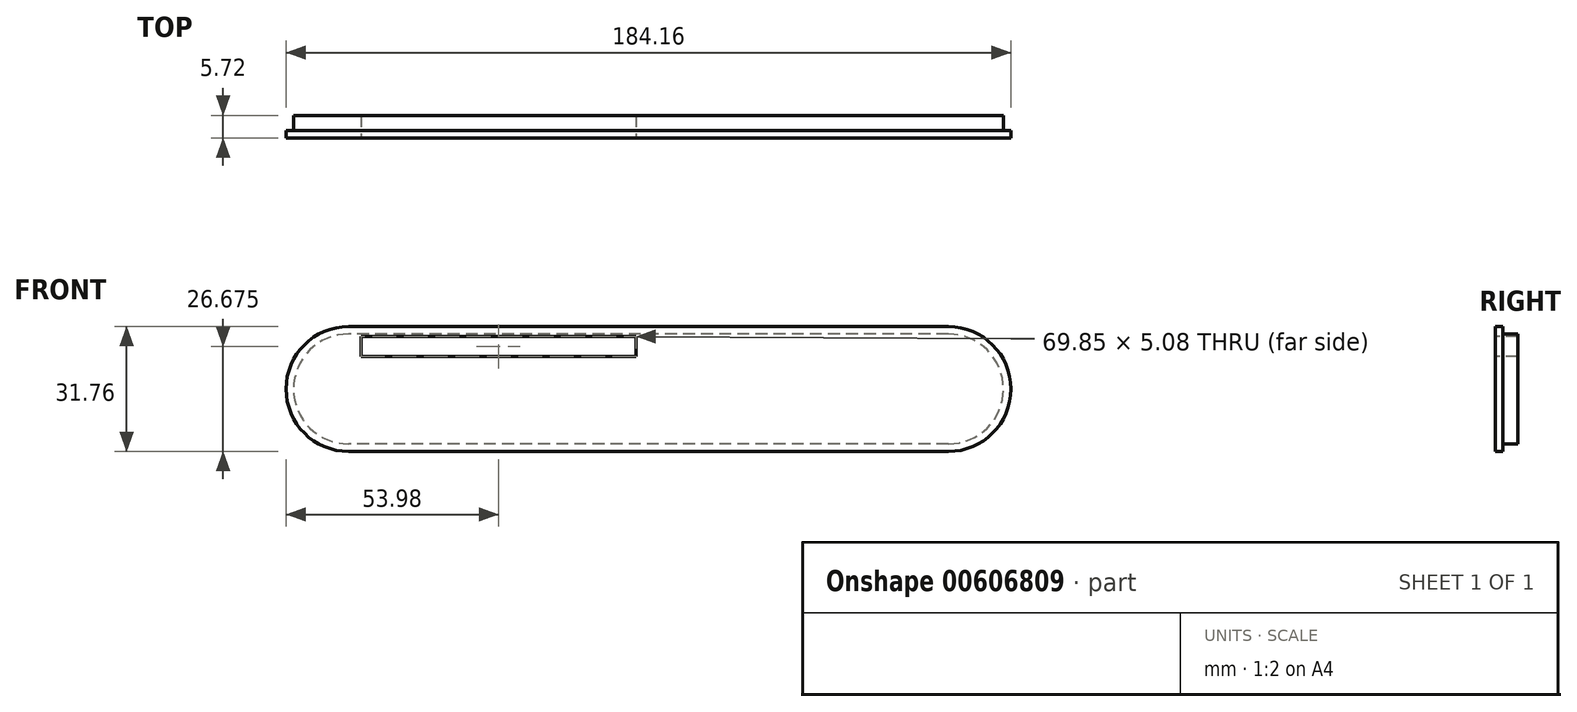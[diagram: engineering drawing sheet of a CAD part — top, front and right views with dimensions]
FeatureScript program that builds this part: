
annotation { "Feature Type Name" : "Feature", "Feature Type Description" : "" }
export const myFeature = defineFeature(function(context is Context, id is Id, definition is map)
    precondition{}
    {
        {
            var Q0;
            Q0=qCreatedBy(makeId("Front.planeOp"),FACE);
            var sketch = newSketch(context, id + "F0", { "sketchPlane" : qUnion([Q0])});
            skLineSegment(sketch, "E0", {"start": v(-76.2, 0) * mm, "end": v(76.2, 0) * mm});
            skLineSegment(sketch, "E1.bottom", {"start": v(76.2, -15.87) * mm, "end": v(-76.2, -15.88) * mm});
            skLineSegment(sketch, "E1.top", {"start": v(76.2, 15.88) * mm, "end": v(-76.2, 15.87) * mm});
            skLineSegment(sketch, "E1.left", {"start": v(76.2, -15.87) * mm, "end": v(76.2, 15.88) * mm});
            skLineSegment(sketch, "E1.right", {"start": v(-76.2, -15.88) * mm, "end": v(-76.2, 15.87) * mm});
            skPoint(sketch, "E1.middle", {"position": v(0, 0) * mm});
            skCircle(sketch, "E2", {"center": v(-76.2, 0) * mm, "radius": 15.88 * mm});
            skCircle(sketch, "E3", {"center": v(76.2, 0) * mm, "radius": 15.88 * mm});
            skSolve(sketch);
        }
        {
            var Q0;
            Q0=qCreatedBy(makeId("Front.planeOp"),FACE);
            var sketch = newSketch(context, id + "F1", { "sketchPlane" : qUnion([Q0])});
            skLineSegment(sketch, "E4.bottom", {"start": v(76.2, 13.97) * mm, "end": v(-76.2, 13.97) * mm});
            skLineSegment(sketch, "E4.top", {"start": v(76.2, -13.97) * mm, "end": v(-76.2, -13.97) * mm});
            skLineSegment(sketch, "E4.left", {"start": v(76.2, 13.97) * mm, "end": v(76.2, -13.97) * mm});
            skLineSegment(sketch, "E4.right", {"start": v(-76.2, 13.97) * mm, "end": v(-76.2, -13.97) * mm});
            skPoint(sketch, "E4.middle", {"position": v(0, 0) * mm});
            skCircle(sketch, "E5", {"center": v(-76.2, 0) * mm, "radius": 13.97 * mm});
            skCircle(sketch, "E6", {"center": v(76.2, 0) * mm, "radius": 13.97 * mm});
            skSolve(sketch);
        }
        {
            var Q0;
            Q0=qSketchRegion(id+"F0",true);
            extrude(context, id + "F2", {"entities" : qUnion([Q0]), "depth" : 1.9 * mm, "offsetDistance" : 25.4 * mm});
        }
        {
            var Q0;
            Q0=qSketchRegion(id+"F1",true);
            extrude(context, id + "F3", {"entities" : qUnion([Q0]), "operationType" : NewBodyOperationType.ADD, "oppositeDirection" : true, "depth" : 3.8 * mm, "offsetDistance" : 25.4 * mm});
        }
        {
            var Q0;
            Q0=makeQuery(id+"F2.opExtrude","CAP_FACE",FACE,{"disambiguationData":[OSD([sQuery(id+"F0.wireOp",EDGE,"E1.bottom"),sQuery(id+"F0.wireOp",EDGE,"E1.top"),sQuery(id+"F0.wireOp",EDGE,"E2"),sQuery(id+"F0.wireOp",EDGE,"E3")])],"isStart":false});
            var sketch = newSketch(context, id + "F4", { "sketchPlane" : qUnion([Q0])});
            skLineSegment(sketch, "E7.bottom", {"start": v(-73.03, 8.25) * mm, "end": v(-3.17, 8.25) * mm});
            skLineSegment(sketch, "E7.top", {"start": v(-73.03, 13.33) * mm, "end": v(-3.17, 13.33) * mm});
            skLineSegment(sketch, "E7.left", {"start": v(-73.03, 8.25) * mm, "end": v(-73.03, 13.33) * mm});
            skLineSegment(sketch, "E7.right", {"start": v(-3.17, 8.25) * mm, "end": v(-3.17, 13.33) * mm});
            skSolve(sketch);
        }
        {
            var Q0;
            Q0=makeQuery(id+"F4.imprint","IMPRINT",FACE,{"disambiguationData":[TD([[makeQuery(id+"F4.imprint","IMPRINT",EDGE,{"derivedFrom":sQuery(id+"F4.wireOp",EDGE,"E7.bottom")}),1.0]])]});
            extrude(context, id + "F5", {"entities" : qUnion([Q0]), "operationType" : NewBodyOperationType.REMOVE, "endBound" : BoundingType.THROUGH_ALL, "oppositeDirection" : true, "depth" : 25.4 * mm, "offsetDistance" : 25.4 * mm});
        }
    });
